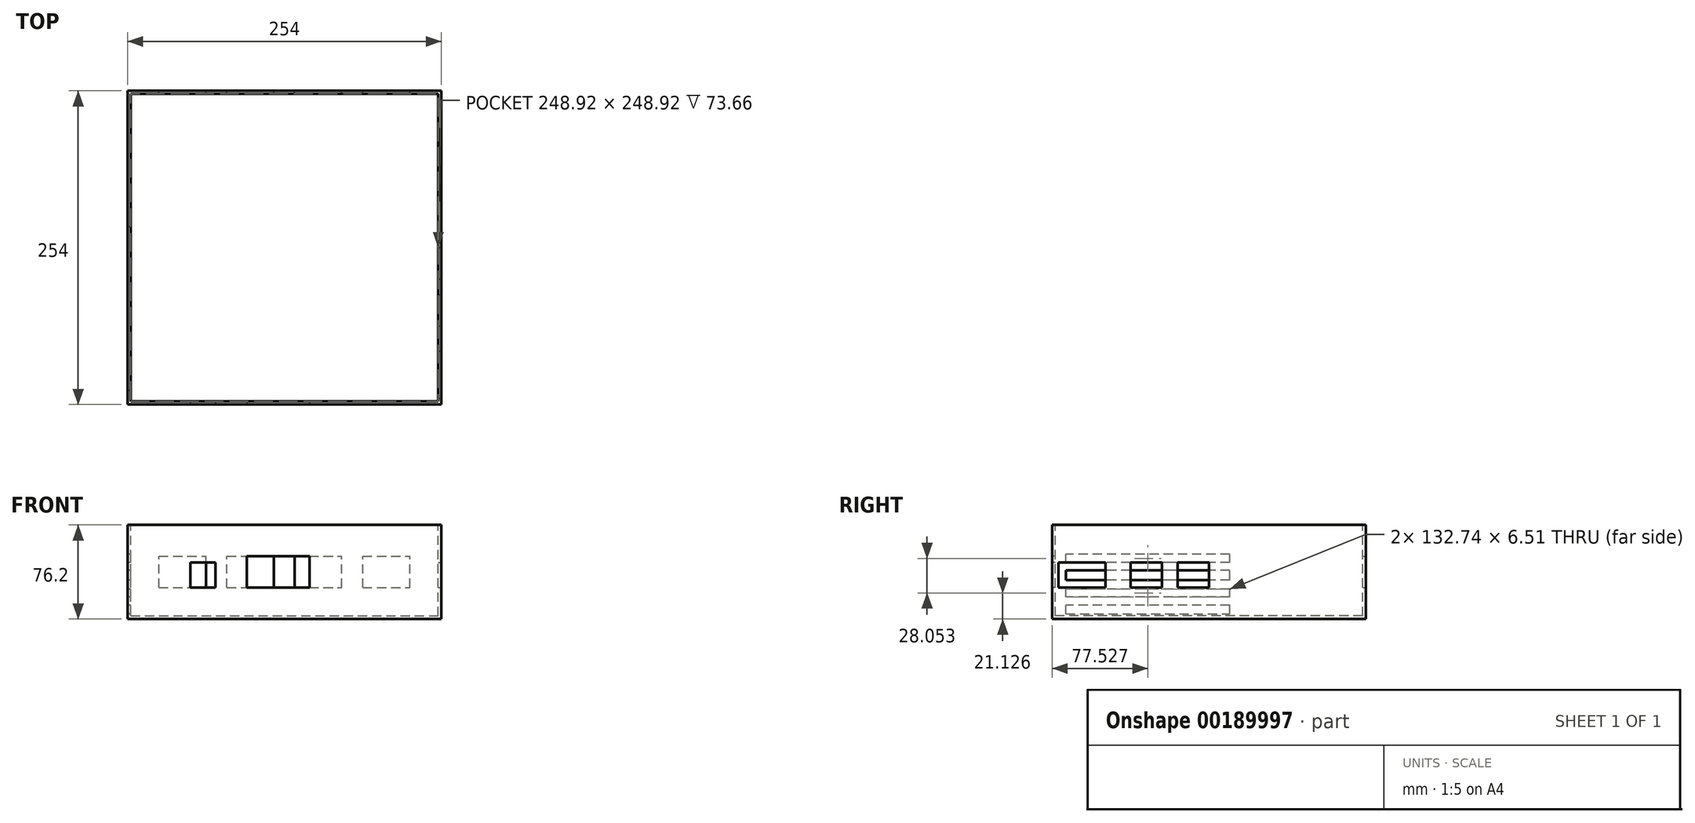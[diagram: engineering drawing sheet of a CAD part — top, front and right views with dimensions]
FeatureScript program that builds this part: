
annotation { "Feature Type Name" : "Feature", "Feature Type Description" : "" }
export const myFeature = defineFeature(function(context is Context, id is Id, definition is map)
    precondition{}
    {
        {
            var Q0;
            Q0=qCreatedBy(makeId("Top.planeOp"),FACE);
            var sketch = newSketch(context, id + "F0", { "sketchPlane" : qUnion([Q0])});
            skLineSegment(sketch, "E0", {"start": v(0, 0) * mm, "end": v(254, 0) * mm});
            skLineSegment(sketch, "E1", {"start": v(254, 0) * mm, "end": v(254, 254) * mm});
            skLineSegment(sketch, "E2", {"start": v(254, 254) * mm, "end": v(0, 254) * mm});
            skLineSegment(sketch, "E3", {"start": v(0, 254) * mm, "end": v(0, 0) * mm});
            skSolve(sketch);
        }
        {
            var Q0;
            Q0=makeQuery(id+"F0.imprint","IMPRINT",FACE,{"disambiguationData":[TD([[makeQuery(id+"F0.imprint","IMPRINT",EDGE,{"derivedFrom":sQuery(id+"F0.wireOp",EDGE,"E0")}),1.0]])]});
            extrude(context, id + "F1", {"entities" : qUnion([Q0]), "depth" : 76.2 * mm});
        }
        {
            var Q0;
            Q0=makeQuery(id+"F1.opExtrude","CAP_FACE",FACE,{"disambiguationData":[OSD([sQuery(id+"F0.wireOp",EDGE,"E0"),sQuery(id+"F0.wireOp",EDGE,"E1"),sQuery(id+"F0.wireOp",EDGE,"E2"),sQuery(id+"F0.wireOp",EDGE,"E3")])],"isStart":false});
            var sketch = newSketch(context, id + "F2", { "sketchPlane" : qUnion([Q0])});
            skLineSegment(sketch, "E4", {"start": v(2.54, 2.54) * mm, "end": v(251.46, 2.54) * mm});
            skLineSegment(sketch, "E5", {"start": v(251.46, 2.54) * mm, "end": v(251.46, 251.46) * mm});
            skLineSegment(sketch, "E6", {"start": v(251.46, 251.46) * mm, "end": v(2.54, 251.46) * mm});
            skLineSegment(sketch, "E7", {"start": v(2.54, 251.46) * mm, "end": v(2.54, 2.54) * mm});
            skSolve(sketch);
        }
        {
            var Q0;
            Q0=makeQuery(id+"F2.imprint","IMPRINT",FACE,{"disambiguationData":[TD([[makeQuery(id+"F2.imprint","IMPRINT",EDGE,{"derivedFrom":sQuery(id+"F2.wireOp",EDGE,"E4")}),1.0]])]});
            extrude(context, id + "F3", {"entities" : qUnion([Q0]), "operationType" : NewBodyOperationType.REMOVE, "oppositeDirection" : true, "depth" : 73.66 * mm});
        }
        {
            var Q0;
            Q0=makeQuery(id+"F1.opExtrude","SWEPT_FACE",FACE,{"disambiguationData":[OSD([sQuery(id+"F0.wireOp",EDGE,"E2")])]});
            var sketch = newSketch(context, id + "F4", { "sketchPlane" : qUnion([Q0])});
            skLineSegment(sketch, "E8.bottom", {"start": v(-25.4, 25.4) * mm, "end": v(-63.5, 25.4) * mm});
            skLineSegment(sketch, "E8.top", {"start": v(-25.4, 50.8) * mm, "end": v(-63.5, 50.8) * mm});
            skLineSegment(sketch, "E8.left", {"start": v(-25.4, 25.4) * mm, "end": v(-25.4, 50.8) * mm});
            skLineSegment(sketch, "E8.right", {"start": v(-63.5, 25.4) * mm, "end": v(-63.5, 50.8) * mm});
            skLineSegment(sketch, "E9.bottom", {"start": v(-80.42, 25.4) * mm, "end": v(-118.52, 25.4) * mm});
            skLineSegment(sketch, "E9.top", {"start": v(-80.42, 50.8) * mm, "end": v(-118.52, 50.8) * mm});
            skLineSegment(sketch, "E9.left", {"start": v(-80.42, 25.4) * mm, "end": v(-80.42, 50.8) * mm});
            skLineSegment(sketch, "E9.right", {"start": v(-118.52, 25.4) * mm, "end": v(-118.52, 50.8) * mm});
            skLineSegment(sketch, "E10.bottom", {"start": v(-135.43, 25.4) * mm, "end": v(-173.53, 25.4) * mm});
            skLineSegment(sketch, "E10.top", {"start": v(-135.43, 50.8) * mm, "end": v(-173.53, 50.8) * mm});
            skLineSegment(sketch, "E10.left", {"start": v(-135.43, 25.4) * mm, "end": v(-135.43, 50.8) * mm});
            skLineSegment(sketch, "E10.right", {"start": v(-173.53, 25.4) * mm, "end": v(-173.53, 50.8) * mm});
            skLineSegment(sketch, "E11.bottom", {"start": v(-190.45, 25.4) * mm, "end": v(-228.55, 25.4) * mm});
            skLineSegment(sketch, "E11.top", {"start": v(-190.45, 50.8) * mm, "end": v(-228.55, 50.8) * mm});
            skLineSegment(sketch, "E11.left", {"start": v(-190.45, 25.4) * mm, "end": v(-190.45, 50.8) * mm});
            skLineSegment(sketch, "E11.right", {"start": v(-228.55, 25.4) * mm, "end": v(-228.55, 50.8) * mm});
            skSolve(sketch);
        }
        {
            var Q0;
            Q0=makeQuery(id+"F4.imprint","IMPRINT",FACE,{"disambiguationData":[TD([[makeQuery(id+"F4.imprint","IMPRINT",EDGE,{"derivedFrom":sQuery(id+"F4.wireOp",EDGE,"E11.bottom")}),-1.0]])]});
            var Q1;
            Q1=makeQuery(id+"F4.imprint","IMPRINT",FACE,{"disambiguationData":[TD([[makeQuery(id+"F4.imprint","IMPRINT",EDGE,{"derivedFrom":sQuery(id+"F4.wireOp",EDGE,"E10.bottom")}),-1.0]])]});
            var Q2;
            Q2=makeQuery(id+"F4.imprint","IMPRINT",FACE,{"disambiguationData":[TD([[makeQuery(id+"F4.imprint","IMPRINT",EDGE,{"derivedFrom":sQuery(id+"F4.wireOp",EDGE,"E9.bottom")}),-1.0]])]});
            var Q3;
            Q3=makeQuery(id+"F4.imprint","IMPRINT",FACE,{"disambiguationData":[TD([[makeQuery(id+"F4.imprint","IMPRINT",EDGE,{"derivedFrom":sQuery(id+"F4.wireOp",EDGE,"E8.bottom")}),-1.0]])]});
            extrude(context, id + "F5", {"entities" : qUnion([Q0, Q1, Q2, Q3]), "operationType" : NewBodyOperationType.REMOVE, "oppositeDirection" : true, "depth" : 25.4 * mm});
        }
        {
            var Q0;
            Q0=makeQuery(id+"F1.opExtrude","SWEPT_FACE",FACE,{"disambiguationData":[OSD([sQuery(id+"F0.wireOp",EDGE,"E1")])]});
            var sketch = newSketch(context, id + "F6", { "sketchPlane" : qUnion([Q0])});
            skLineSegment(sketch, "E12.bottom", {"start": v(127, 25.4) * mm, "end": v(101.6, 25.4) * mm});
            skLineSegment(sketch, "E12.top", {"start": v(127, 45.98) * mm, "end": v(101.6, 45.98) * mm});
            skLineSegment(sketch, "E12.left", {"start": v(127, 25.4) * mm, "end": v(127, 45.98) * mm});
            skLineSegment(sketch, "E12.right", {"start": v(101.6, 25.4) * mm, "end": v(101.6, 45.98) * mm});
            skLineSegment(sketch, "E13.bottom", {"start": v(88.9, 25.4) * mm, "end": v(63.5, 25.4) * mm});
            skLineSegment(sketch, "E13.top", {"start": v(88.9, 45.98) * mm, "end": v(63.5, 45.98) * mm});
            skLineSegment(sketch, "E13.left", {"start": v(88.9, 25.4) * mm, "end": v(88.9, 45.98) * mm});
            skLineSegment(sketch, "E13.right", {"start": v(63.5, 25.4) * mm, "end": v(63.5, 45.98) * mm});
            skLineSegment(sketch, "E14.bottom", {"start": v(43.18, 25.4) * mm, "end": v(5.08, 25.4) * mm});
            skLineSegment(sketch, "E14.top", {"start": v(43.18, 45.98) * mm, "end": v(5.08, 45.98) * mm});
            skLineSegment(sketch, "E14.left", {"start": v(43.18, 25.4) * mm, "end": v(43.18, 45.98) * mm});
            skLineSegment(sketch, "E14.right", {"start": v(5.08, 25.4) * mm, "end": v(5.08, 45.98) * mm});
            skPoint(sketch, "E15.start.orphan", {"position": v(127, 0) * mm});
            skSolve(sketch);
        }
        {
            var Q0;
            Q0=makeQuery(id+"F6.imprint","IMPRINT",FACE,{"disambiguationData":[TD([[makeQuery(id+"F6.imprint","IMPRINT",EDGE,{"derivedFrom":sQuery(id+"F6.wireOp",EDGE,"E14.bottom")}),-1.0]])]});
            var Q1;
            Q1=makeQuery(id+"F6.imprint","IMPRINT",FACE,{"disambiguationData":[TD([[makeQuery(id+"F6.imprint","IMPRINT",EDGE,{"derivedFrom":sQuery(id+"F6.wireOp",EDGE,"E13.bottom")}),-1.0]])]});
            var Q2;
            Q2=makeQuery(id+"F6.imprint","IMPRINT",FACE,{"disambiguationData":[TD([[makeQuery(id+"F6.imprint","IMPRINT",EDGE,{"derivedFrom":sQuery(id+"F6.wireOp",EDGE,"E12.bottom")}),-1.0]])]});
            extrude(context, id + "F7", {"entities" : qUnion([Q0, Q1, Q2]), "operationType" : NewBodyOperationType.REMOVE, "oppositeDirection" : true, "depth" : 25.4 * mm});
        }
        {
            var Q0;
            Q0=makeQuery(id+"F1.opExtrude","SWEPT_FACE",FACE,{"disambiguationData":[OSD([sQuery(id+"F0.wireOp",EDGE,"E0")])]});
            var sketch = newSketch(context, id + "F8", { "sketchPlane" : qUnion([Q0])});
            skLineSegment(sketch, "E16.bottom", {"start": v(50.8, 25.4) * mm, "end": v(71.12, 25.4) * mm});
            skLineSegment(sketch, "E16.top", {"start": v(50.8, 45.72) * mm, "end": v(71.12, 45.72) * mm});
            skLineSegment(sketch, "E16.left", {"start": v(50.8, 25.4) * mm, "end": v(50.8, 45.72) * mm});
            skLineSegment(sketch, "E16.right", {"start": v(71.12, 25.4) * mm, "end": v(71.12, 45.72) * mm});
            skLineSegment(sketch, "E17.bottom", {"start": v(96.52, 25.4) * mm, "end": v(147.32, 25.4) * mm});
            skLineSegment(sketch, "E17.top", {"start": v(96.52, 50.8) * mm, "end": v(147.32, 50.8) * mm});
            skLineSegment(sketch, "E17.left", {"start": v(96.52, 25.4) * mm, "end": v(96.52, 50.8) * mm});
            skLineSegment(sketch, "E17.right", {"start": v(147.32, 25.4) * mm, "end": v(147.32, 50.8) * mm});
            skSolve(sketch);
        }
        {
            var Q0;
            Q0=makeQuery(id+"F8.imprint","IMPRINT",FACE,{"disambiguationData":[TD([[makeQuery(id+"F8.imprint","IMPRINT",EDGE,{"derivedFrom":sQuery(id+"F8.wireOp",EDGE,"E16.bottom")}),1.0]])]});
            var Q1;
            Q1=makeQuery(id+"F8.imprint","IMPRINT",FACE,{"disambiguationData":[TD([[makeQuery(id+"F8.imprint","IMPRINT",EDGE,{"derivedFrom":sQuery(id+"F8.wireOp",EDGE,"E17.bottom")}),1.0]])]});
            extrude(context, id + "F9", {"entities" : qUnion([Q0, Q1]), "operationType" : NewBodyOperationType.REMOVE, "oppositeDirection" : true, "depth" : 25.4 * mm});
        }
        {
            var Q0;
            Q0=makeQuery(id+"F1.opExtrude","SWEPT_FACE",FACE,{"disambiguationData":[OSD([sQuery(id+"F0.wireOp",EDGE,"E3")])]});
            var sketch = newSketch(context, id + "F10", { "sketchPlane" : qUnion([Q0])});
            skLineSegment(sketch, "E18.bottom", {"start": v(-11.16, 4.32) * mm, "end": v(-143.9, 4.32) * mm});
            skLineSegment(sketch, "E18.top", {"start": v(-11.16, 58.92) * mm, "end": v(-143.9, 58.92) * mm});
            skLineSegment(sketch, "E18.left", {"start": v(-11.16, 4.32) * mm, "end": v(-11.16, 11.1) * mm});
            skLineSegment(sketch, "E18.right", {"start": v(-143.9, 4.32) * mm, "end": v(-143.9, 11.1) * mm});
            skLineSegment(sketch, "E19", {"start": v(-143.9, 52.43) * mm, "end": v(-11.16, 52.43) * mm});
            skLineSegment(sketch, "E20", {"start": v(-143.9, 45.92) * mm, "end": v(-11.16, 45.92) * mm});
            skLineSegment(sketch, "E21", {"start": v(-143.9, 39.41) * mm, "end": v(-11.16, 39.41) * mm});
            skLineSegment(sketch, "E22", {"start": v(-143.9, 31.62) * mm, "end": v(-11.16, 31.62) * mm});
            skLineSegment(sketch, "E23", {"start": v(-143.9, 11.1) * mm, "end": v(-11.16, 11.1) * mm});
            skLineSegment(sketch, "E24", {"start": v(-143.9, 24.38) * mm, "end": v(-11.16, 24.38) * mm});
            skLineSegment(sketch, "E25", {"start": v(-143.9, 17.87) * mm, "end": v(-11.16, 17.87) * mm});
            skLineSegment(sketch, "E26.bottom", {"start": v(-143.9, 58.92) * mm, "end": v(-11.16, 58.92) * mm});
            skLineSegment(sketch, "E26.top", {"start": v(-143.9, 64.96) * mm, "end": v(-11.16, 64.96) * mm});
            skLineSegment(sketch, "E26.left", {"start": v(-143.9, 58.92) * mm, "end": v(-143.9, 64.96) * mm});
            skLineSegment(sketch, "E26.right", {"start": v(-11.16, 58.92) * mm, "end": v(-11.16, 64.96) * mm});
            skLineSegment(sketch, "E27.trimOffspring", {"start": v(-143.9, 17.87) * mm, "end": v(-143.9, 24.38) * mm});
            skLineSegment(sketch, "E28.trimOffspring", {"start": v(-143.9, 31.62) * mm, "end": v(-143.9, 39.41) * mm});
            skLineSegment(sketch, "E29.trimOffspring", {"start": v(-143.9, 45.92) * mm, "end": v(-143.9, 52.43) * mm});
            skLineSegment(sketch, "E30.trimOffspring", {"start": v(-11.16, 45.92) * mm, "end": v(-11.16, 52.43) * mm});
            skLineSegment(sketch, "E31.trimOffspring", {"start": v(-11.16, 31.62) * mm, "end": v(-11.16, 39.41) * mm});
            skLineSegment(sketch, "E32.trimOffspring", {"start": v(-11.16, 17.87) * mm, "end": v(-11.16, 24.38) * mm});
            skSolve(sketch);
        }
        {
            var Q0;
            Q0=makeQuery(id+"F10.imprint","IMPRINT",FACE,{"disambiguationData":[TD([[makeQuery(id+"F10.imprint","IMPRINT",EDGE,{"derivedFrom":sQuery(id+"F10.wireOp",EDGE,"E26.bottom")}),1.0]])]});
            var Q1;
            Q1=makeQuery(id+"F10.imprint","IMPRINT",FACE,{"disambiguationData":[TD([[makeQuery(id+"F10.imprint","IMPRINT",EDGE,{"derivedFrom":sQuery(id+"F10.wireOp",EDGE,"E19")}),-1.0]])]});
            var Q2;
            Q2=makeQuery(id+"F10.imprint","IMPRINT",FACE,{"disambiguationData":[TD([[makeQuery(id+"F10.imprint","IMPRINT",EDGE,{"derivedFrom":sQuery(id+"F10.wireOp",EDGE,"E21")}),-1.0]])]});
            var Q3;
            Q3=makeQuery(id+"F10.imprint","IMPRINT",FACE,{"disambiguationData":[TD([[makeQuery(id+"F10.imprint","IMPRINT",EDGE,{"derivedFrom":sQuery(id+"F10.wireOp",EDGE,"E24")}),-1.0]])]});
            var Q4;
            Q4=makeQuery(id+"F10.imprint","IMPRINT",FACE,{"disambiguationData":[TD([[makeQuery(id+"F10.imprint","IMPRINT",EDGE,{"derivedFrom":sQuery(id+"F10.wireOp",EDGE,"E18.bottom")}),-1.0]])]});
            extrude(context, id + "F11", {"entities" : qUnion([Q0, Q1, Q2, Q3, Q4]), "operationType" : NewBodyOperationType.REMOVE, "oppositeDirection" : true, "depth" : 25.4 * mm});
        }
    });
